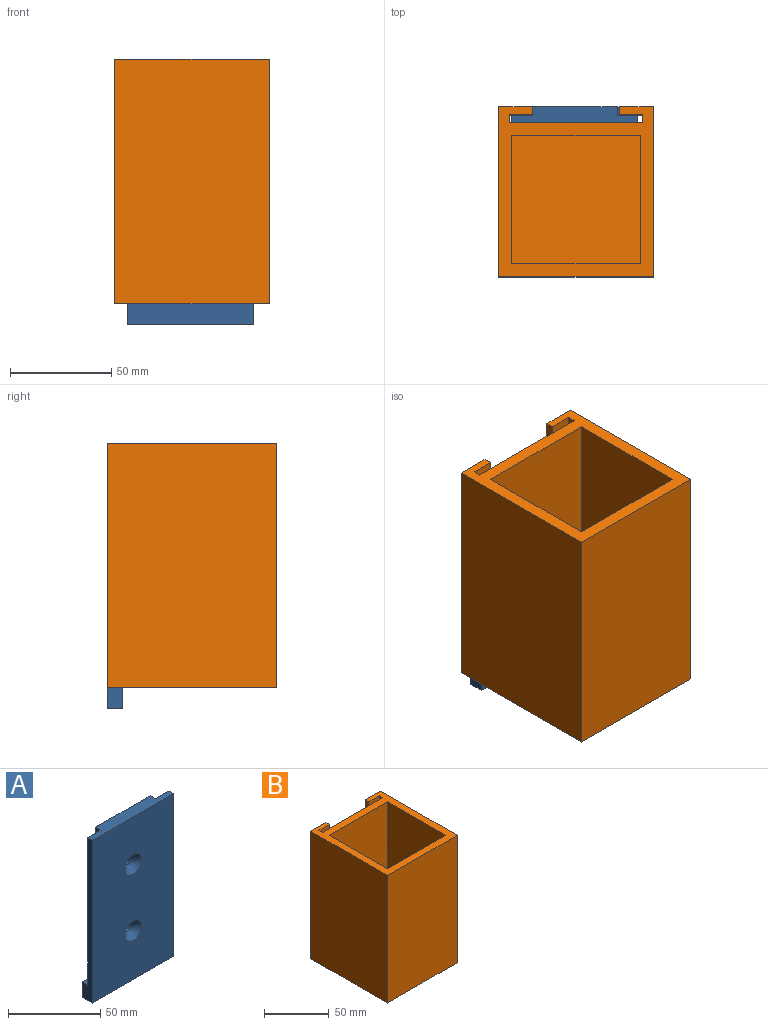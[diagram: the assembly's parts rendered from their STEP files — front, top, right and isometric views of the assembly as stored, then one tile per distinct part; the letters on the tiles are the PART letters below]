
ASSEMBLY  parts=2 mates=1
PART A: 16 faces, bbox 62.2x7.6x108 mm
  f0: plane 107.95x62.23mm, normal (0,-1,0), area 6448.9mm2, adj f1,f7,f8,f9,f14,f15
  f1: plane 107.95x7.62mm, normal (1,0,0), area 425.2mm2, adj f0,f2,f4,f8,f9,f10
  f2: plane 97.79x10.16mm, normal (0,1,0), area 993.5mm2, adj f1,f3,f8,f10
  f3: plane 97.79x4.06mm, normal (1,0,0), area 397.4mm2, adj f2,f4,f8,f10
  f4: plane 107.95x62.23mm, normal (0,1,0), area 4705.5mm2, adj f1,f3,f5,f7,f8,f9,f10,f11
  f5: plane 97.79x4.06mm, normal (-1,0,0), area 397.4mm2, adj f4,f6,f8,f11
  f6: plane 97.79x10.16mm, normal (0,1,0), area 993.5mm2, adj f5,f7,f8,f11
  f7: plane 107.95x7.62mm, normal (-1,0,0), area 425.2mm2, adj f0,f4,f6,f8,f9,f11
  f8: plane 62.23x7.62mm, normal (0,0,1), area 391.6mm2, adj f0,f1,f2,f3,f4,f5,f6,f7
  f9: plane 62.23x7.62mm, normal (0,0,-1), area 474.2mm2, adj f0,f1,f4,f7
  f10: plane 10.16x4.06mm, normal (0,0,1), area 41.3mm2, adj f1,f2,f3,f4
  f11: plane 10.16x4.06mm, normal (0,0,1), area 41.3mm2, adj f4,f5,f6,f7
  f12: cylinder r=2mm len=4mm, axis (0,-1,0), area 47.9mm2, adj f4,f15
  f13: cylinder r=2mm len=4mm, axis (0,-1,0), area 47.9mm2, adj f4,f14
  f14: cone r=2mm half-angle=50deg, axis (0,-1,0), area 159mm2, adj f0,f13
  f15: cone r=2mm half-angle=50deg, axis (0,-1,0), area 159mm2, adj f0,f12
PART B: 19 faces, bbox 76.2x83.8x120.7 mm
  f0: plane 120.65x66.04mm, normal (0,1,0), area 7967.7mm2, adj f4,f8,f9,f17
  f1: plane 120.65x83.82mm, normal (-1,0,0), area 10112.9mm2, adj f2,f4,f12,f17
  f2: plane 120.65x76.2mm, normal (0,-1,0), area 9193.5mm2, adj f1,f3,f4,f17
  f3: plane 120.65x83.82mm, normal (1,0,0), area 10112.9mm2, adj f2,f4,f5,f17
  f4: plane 83.82x76.2mm, normal (0,0,-1), area 5971mm2, adj f0,f1,f2,f3,f5,f6,f7,f8
  f5: plane 120.65x16.51mm, normal (0,1,0), area 1991.9mm2, adj f3,f4,f6,f17
  f6: plane 120.65x3.81mm, normal (-1,0,0), area 459.7mm2, adj f4,f5,f7,f17
  f7: plane 120.65x11.43mm, normal (0,-1,0), area 1379mm2, adj f4,f6,f8,f17
  f8: plane 120.65x3.81mm, normal (-1,0,0), area 459.7mm2, adj f0,f4,f7,f17
  f9: plane 120.65x3.81mm, normal (1,0,0), area 459.7mm2, adj f0,f4,f10,f17
  f10: plane 120.65x11.43mm, normal (0,-1,0), area 1379mm2, adj f4,f9,f11,f17
  f11: plane 120.65x3.81mm, normal (1,0,0), area 459.7mm2, adj f4,f10,f12,f17
  f12: plane 120.65x16.51mm, normal (0,1,0), area 1991.9mm2, adj f1,f4,f11,f17
  f13: plane 114.3x63.5mm, normal (-1,0,0), area 7258mm2, adj f14,f16,f17,f18
  f14: plane 114.3x63.5mm, normal (0,1,0), area 7258.1mm2, adj f13,f15,f17,f18
  f15: plane 114.3x63.5mm, normal (1,0,0), area 7258mm2, adj f14,f16,f17,f18
  f16: plane 114.3x63.5mm, normal (0,-1,0), area 7258.1mm2, adj f13,f15,f17,f18
  f17: plane 83.82x76.2mm, normal (0,0,1), area 1938.7mm2, adj f0,f1,f2,f3,f5,f6,f7,f8
  f18: plane 63.5x63.5mm, normal (0,0,1), area 4032.3mm2, adj f13,f14,f15,f16
PLACE A t=(0.12,40.49,-10.17)mm
PLACE B t=(0.75,2.39,-0.01)mm
MATE fastened A.f11 <-> B.f4  axis (0,0,1) through (-20.84,48.11,-0.01)mm
